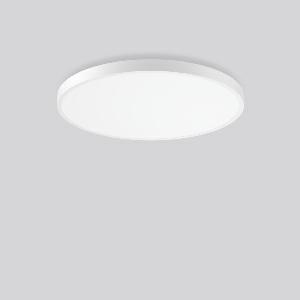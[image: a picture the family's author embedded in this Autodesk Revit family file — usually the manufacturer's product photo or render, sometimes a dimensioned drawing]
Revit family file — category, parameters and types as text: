
# Revit family: triona_round_a_312387_002_1_730_2ecf
name_source: partatom
category: Lighting Fixtures
units: mm (PartAtom-declared; Revit-internal decimal feet)

## family parameters
Cut with Voids When Loaded = No
Host = Face
Light Source = No
Part Type = Normal
Room Calculation Point = No
Round Connector Dimension = Use Diameter
Shared = No

## types (1)
- TRIONA round A (1 x LED Modul 840, 8300 lm, 4000)
    Apparent Load = 80 VA
    CIE Flux Codes = 49 80 96 100 100
    Color Rendering = 80
    Color Temperature = 4000
    Default Elevation = 1800 mm
    Description = Series: TRIONA round
Decorative round LED surface-mounted luminaire. Flat, seamless frame: aluminium extrusion profile, powder coated. Cover made of sheet steel, powder-coated. Light emission through a diffuser: plastic, opal. Lightguide and diffuser made of non-yellowing plastic (PMMA). Lateral light emission (RZB SIDELITE technology) for above-average homogeneous light distribution. Suitable for Ceiling mounting, Wall (surface). Tool-free mounting via bayonet connection. Electronic ballast included. Very easy installation thanks to Plug+Play connection. With Casambi smart+free Bluetooth control for wireless network and operation using Android / iOS devices, free app available for download. 
Colour: traffic white, matt (RAL 9016)
Diameter: 845 mm
Height: 88 mm
Lamp: LED
Socket: without socket
Colour temperature: 4000K
Colour rendering index (CRI): 80
System power: 80 W
Rated luminous flux: 8300 lm
Luminous efficiency: 104 lm/W
Control gear: Dimmable Bluetooth converter
Protection class: I
Type of protection: IP 20
    Height = 88 mm
    Lamp = 1 x LED Modul 840
    Lamp Light Flux = 8300 lm
    Lamp count = 1
    Length = 845 mm
    Lifetime = 50000 h
    Luminous efficacy = 104 lm/W
    Manufacturer = RZB
    ModVariant = No
    Model = 312387.002.1.730
    Mounting Place = Ceiling
    Mounting Type = Surface mounted
    Number of Poles = 1
    OnlyDefault = Yes
    Power Factor = 1
    Product Name = TRIONA round A
    Product group = Surface mounted modular luminaires
    ProductGroupID = 306
    Protection Class = Protection class I
    Protection Degree = IP 20
    RLX_Detail_Level = 1
    RLX_Emergency_Light_Flux = 0 lm
    RLX_Emergency_Type = 0
    RLX_Emergency_Type_DB = No
    RlxData = <blob elided: 32813 chars, md5=cf737710>
    Socket = socket
    Standby Power = 0 W
    System Light Flux = 8300 lm
    System Power = 80 W
    Type Comments = Product without accessories
    Type Image = 312388.002.jpg
    URL = http://relux.com
    VarID = ---
    Voltage = 230 V
    Voltage Range = 220-240 V
    Weight = 0.00 kg
    Width = 0 mm  [stored 0 ft]

note: [stored X ft] marks values corroborated as IEEE doubles in the binary element streams (Revit-internal decimal feet)

## geometry (parser evidence)
native form markers: Blend x4, Sweep x10
no freeform markers — native parametric forms only
